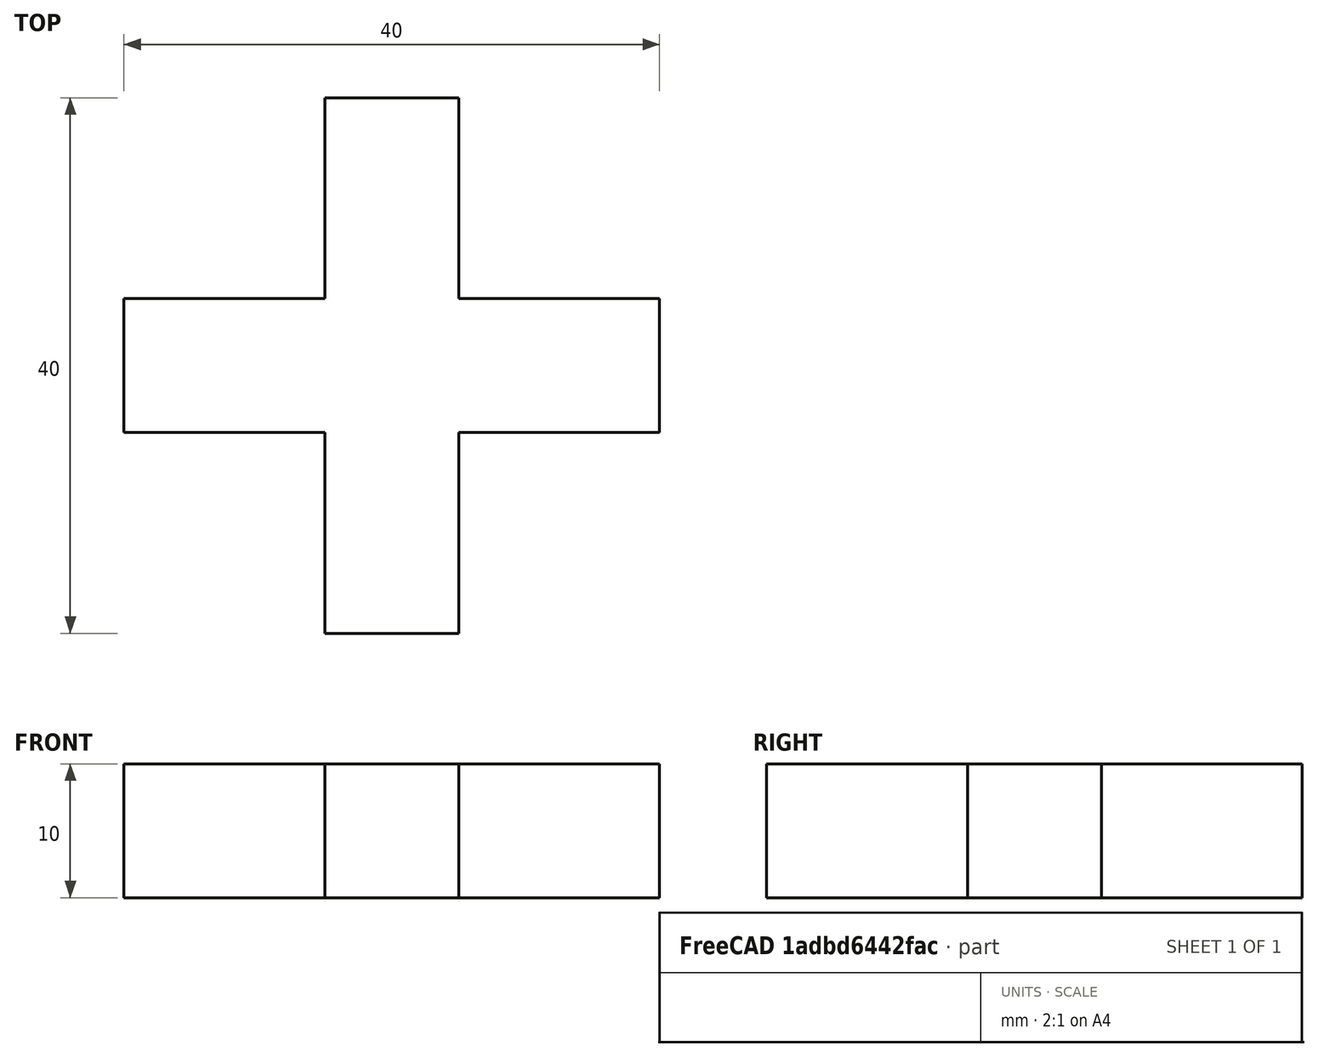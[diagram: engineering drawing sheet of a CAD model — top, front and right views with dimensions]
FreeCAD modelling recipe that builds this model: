
FCSTD DOCUMENT  (FreeCAD 0.17R13217 (Git))
Label: 05-pieza-cruz
License: All rights reserved
LicenseURL: http://en.wikipedia.org/wiki/All_rights_reserved
objects: Sketcher::SketchObject×1, PartDesign::Pad×1, PartDesign::Body×1
note: 4 computed .brp shape members not serialized (recipe doc carries the construction recipe); baked Part::Feature solids carry a one-line shape summary decoded from their .brp

FEATURE [Sketcher::SketchObject] Sketch
  MapMode = 5
  Support = -> [XY_Plane]
  sketch-geometry (12):
    g0: LineSegment StartX=-5 StartY=20 StartZ=0 EndX=5 EndY=20 EndZ=0
    g1: LineSegment StartX=5 StartY=20 StartZ=0 EndX=5 EndY=5 EndZ=0
    g2: LineSegment StartX=5 StartY=5 StartZ=0 EndX=20 EndY=5 EndZ=0
    g3: LineSegment StartX=20 StartY=5 StartZ=0 EndX=20 EndY=-5 EndZ=0
    g4: LineSegment StartX=20 StartY=-5 StartZ=0 EndX=5 EndY=-5 EndZ=0
    g5: LineSegment StartX=5 StartY=-5 StartZ=0 EndX=5 EndY=-20 EndZ=0
    g6: LineSegment StartX=5 StartY=-20 StartZ=0 EndX=-5 EndY=-20 EndZ=0
    g7: LineSegment StartX=-5 StartY=-20 StartZ=0 EndX=-5 EndY=-5 EndZ=0
    g8: LineSegment StartX=-5 StartY=-5 StartZ=0 EndX=-20 EndY=-5 EndZ=0
    g9: LineSegment StartX=-20 StartY=-5 StartZ=0 EndX=-20 EndY=5 EndZ=0
    g10: LineSegment StartX=-20 StartY=5 StartZ=0 EndX=-5 EndY=5 EndZ=0
    g11: LineSegment StartX=-5 StartY=5 StartZ=0 EndX=-5 EndY=20 EndZ=0
  constraints (35):
    c: Horizontal(g0)
    c: Coincident(g0,g1)
    c: Vertical(g1)
    c: Coincident(g1,g2)
    c: Horizontal(g2)
    c: Coincident(g2,g3)
    c: Vertical(g3)
    c: Coincident(g3,g4)
    c: Horizontal(g4)
    c: Coincident(g4,g5)
    c: Vertical(g5)
    c: Coincident(g5,g6)
    c: Horizontal(g6)
    c: Coincident(g6,g7)
    c: Vertical(g7)
    c: Coincident(g7,g8)
    c: Horizontal(g8)
    c: Coincident(g8,g9)
    c: Vertical(g9)
    c: Coincident(g9,g10)
    c: Horizontal(g10)
    c: Coincident(g10,g11)
    c: Coincident(g11,g0)
    c: Vertical(g11)
    c: Symmetric(g0,g0,g-2)
    c: Symmetric(g9,g2,g-2)
    c: Symmetric(g9,g8,g-1)
    c: PointOnObject(g7,g11)
    c: PointOnObject(g4,g1)
    c: PointOnObject(g4,g8)
    c: Equal(g9,g0)
    c: Equal(g10,g11)
    c: Symmetric(g6,g0,g-1)
    c: DistanceY(g9,g9) = 10
    c: DistanceX(g9,g2) = 40
FEATURE [PartDesign::Pad] Pad
  Length = 10
  Length2 = 100
  Profile = -> Sketch
  Refine = true
  Type = 0
FEATURE [PartDesign::Body] Body
  Group = -> [Sketch,Pad]
  Origin = -> Origin
  Tip = -> Pad
